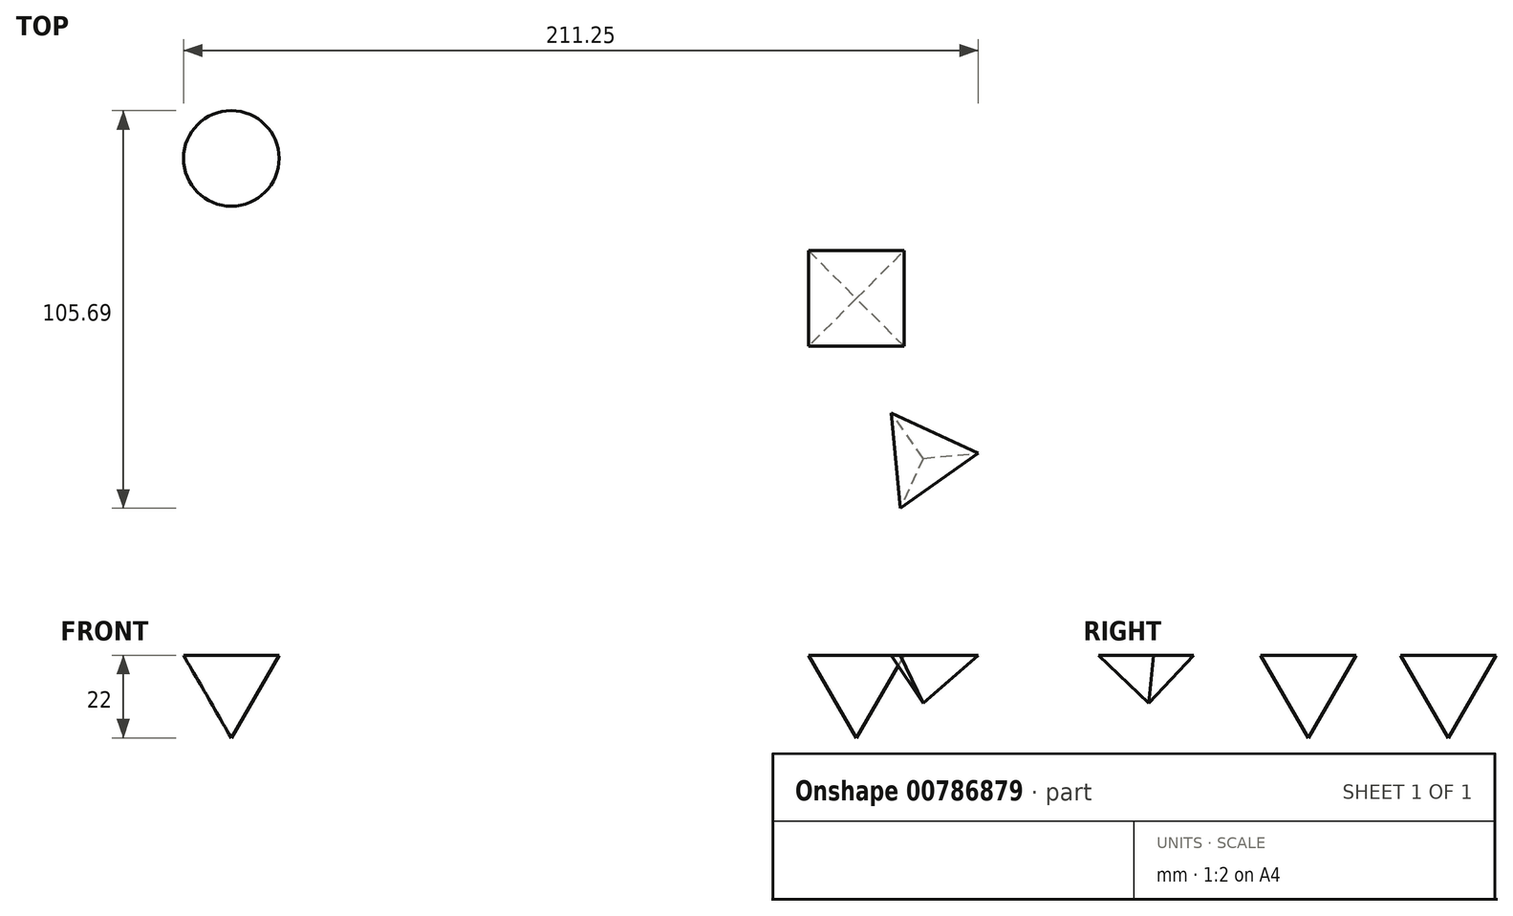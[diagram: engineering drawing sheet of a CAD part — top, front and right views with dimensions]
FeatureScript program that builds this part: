
annotation { "Feature Type Name" : "Feature", "Feature Type Description" : "" }
export const myFeature = defineFeature(function(context is Context, id is Id, definition is map)
    precondition{}
    {
        {
            var Q0;
            Q0=qCreatedBy(makeId("Top.planeOp"),FACE);
            var sketch = newSketch(context, id + "F0", { "sketchPlane" : qUnion([Q0])});
            skLineSegment(sketch, "E0.bottom", {"start": v(0, 25.4) * mm, "end": v(25.4, 25.4) * mm});
            skLineSegment(sketch, "E0.top", {"start": v(0, 0) * mm, "end": v(25.4, 0) * mm});
            skLineSegment(sketch, "E0.left", {"start": v(0, 25.4) * mm, "end": v(0, 0) * mm});
            skLineSegment(sketch, "E0.right", {"start": v(25.4, 25.4) * mm, "end": v(25.4, 0) * mm});
            skCircle(sketch, "E1.cCircle", {"center": v(30.5, -29.74) * mm, "radius": 14.66 * mm, "construction": true});
            skLineSegment(sketch, "E1.0", {"start": v(22.04, -17.77) * mm, "end": v(45.11, -28.4) * mm});
            skLineSegment(sketch, "E1.1", {"start": v(45.11, -28.4) * mm, "end": v(24.37, -43.06) * mm});
            skLineSegment(sketch, "E1.2", {"start": v(24.37, -43.06) * mm, "end": v(22.04, -17.77) * mm});
            skCircle(sketch, "E2", {"center": v(-153.44, 49.93) * mm, "radius": 12.7 * mm});
            skSolve(sketch);
        }
        {
            var Q0;
            Q0=makeQuery(id+"F0.imprint","IMPRINT",FACE,{"disambiguationData":[TD([[makeQuery(id+"F0.imprint","IMPRINT",EDGE,{"derivedFrom":sQuery(id+"F0.wireOp",EDGE,"E0.bottom")}),-1.0]])]});
            var Q1;
            Q1=makeQuery(id+"F0.imprint","IMPRINT",FACE,{"disambiguationData":[TD([[makeQuery(id+"F0.imprint","IMPRINT",EDGE,{"derivedFrom":sQuery(id+"F0.wireOp",EDGE,"E1.0")}),-1.0]])]});
            var Q2;
            Q2=makeQuery(id+"F0.imprint","IMPRINT",FACE,{"disambiguationData":[TD([[makeQuery(id+"F0.imprint","IMPRINT",EDGE,{"derivedFrom":sQuery(id+"F0.wireOp",EDGE,"E2")}),1.0]])]});
            extrude(context, id + "F1", {"entities" : qUnion([Q0, Q1, Q2]), "oppositeDirection" : true, "depth" : 25.4 * mm, "offsetDistance" : 25.4 * mm, "hasDraft" : true, "draftAngle" : 30 * degree, "draftPullDirection" : true});
        }
    });
